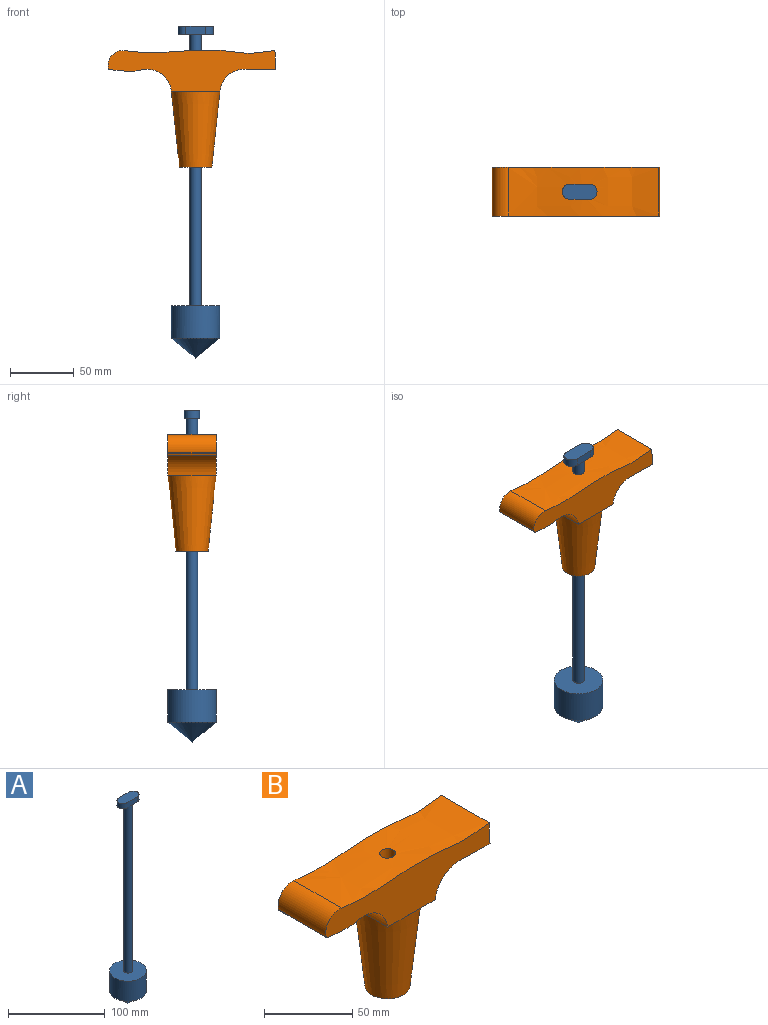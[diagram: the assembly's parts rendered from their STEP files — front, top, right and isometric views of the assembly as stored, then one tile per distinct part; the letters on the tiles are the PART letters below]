
ASSEMBLY  parts=2 mates=2
PART A: 10 faces, bbox 38.1x38.1x260.4 mm
  f0: cylinder r=4.45mm len=212.99mm, axis (0,0,-1), area 5948.5mm2, adj f1,f9
  f1: plane 38.1x38.1mm, normal (0,0,1), area 1078mm2, adj f0,f2
  f2: cylinder r=19.05mm len=38.1mm, axis (0,0,-1), area 3040.2mm2, adj f1,f3
  f3: cone r=19.05mm half-angle=50.7deg, axis (0,0,1), area 1474mm2, adj f2
  f4: plane 15.24x6.35mm, normal (0,1,0), area 96.8mm2, adj f5,f7,f8,f9
  f5: cylinder r=6.04mm len=12.09mm, axis (0,0,-1), area 120.5mm2, adj f4,f6,f8,f9
  f6: plane 15.24x6.35mm, normal (0,-1,0), area 96.8mm2, adj f5,f7,f8,f9
  f7: cylinder r=6.04mm len=12.09mm, axis (0,0,-1), area 120.5mm2, adj f4,f6,f8,f9
  f8: plane 27.33x12.09mm, normal (0,0,1), area 298.9mm2, adj f4,f5,f6,f7
  f9: plane 27.33x12.09mm, normal (0,0,-1), area 236.8mm2, adj f0,f4,f5,f6,f7
PART B: 17 faces, bbox 131.4x38.1x92.1 mm
  f0: cone r=12.7mm half-angle=6.1deg, axis (0,0,1), area 5985.2mm2, adj f1,f2,f3,f4,f5
  f1: plane 25.4x25.4mm, normal (0,0,-1), area 444.6mm2, adj f0,f16
  f2: plane 19.05x19.05mm, normal (0,0,-1), area 77.9mm2, adj f0,f6,f15
  f3: plane 19.05x19.05mm, normal (0,0,-1), area 77.9mm2, adj f0,f13,f15
  f4: plane 19.05x19.05mm, normal (0,0,-1), area 77.9mm2, adj f0,f13,f14
  f5: plane 19.05x19.05mm, normal (0,0,-1), area 77.9mm2, adj f0,f6,f14
  f6: cylinder r=19.21mm len=38.1mm, axis (0,1,0), area 1125.9mm2, adj f2,f5,f7,f14,f15
  f7: plane 38.1x23.33mm, normal (-0.01,0,-1), area 888.8mm2, adj f6,f8,f14,f15
  f8: plane 38.1x14.9mm, normal (1,0,0.05), area 568.2mm2, adj f7,f9,f14,f15
  f9: extruded ~118.17x38.1mm, area 4454.6mm2, adj f8,f10,f14,f15,f16
  f10: cylinder r=11.32mm len=38.1mm, axis (0,1,0), area 826.4mm2, adj f9,f11,f14,f15
  f11: cylinder r=1.27mm len=38.1mm, axis (0,1,0), area 58.1mm2, adj f10,f12,f14,f15
  f12: extruded ~38.1x27.62mm, area 1060.6mm2, adj f11,f13,f14,f15
  f13: cylinder r=19.21mm len=38.1mm, axis (0,1,0), area 1125.9mm2, adj f3,f4,f12,f14,f15
  f14: plane 131.45x32.43mm, normal (0,-1,0), area 2635.9mm2, adj f4,f5,f6,f7,f8,f9,f10,f11
  f15: plane 131.45x32.43mm, normal (0,1,0), area 2635.9mm2, adj f2,f3,f6,f7,f8,f9,f10,f11
  f16: cylinder r=4.45mm len=91.85mm, axis (0,0,-1), area 2561.3mm2, adj f1,f9
PLACE A t=(58.17,-46.52,44.49)mm
PLACE B t=(58.17,-46.52,-59.84)mm
MATE cylindrical A.f0 <-> B.f0  axis (0,0,-1) through (58.17,-46.52,-62.01)mm
MATE slider A.f0 <-> B.f0  axis (0,0,-1) through (58.17,-46.52,-62.01)mm
